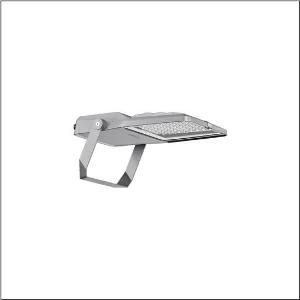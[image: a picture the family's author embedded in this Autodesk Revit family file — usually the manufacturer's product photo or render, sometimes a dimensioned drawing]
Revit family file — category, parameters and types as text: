
# Revit family: floodlight_fl_21_iq_mini___pl52_5xa7771c4d1a_1f8c
name_source: partatom
category: Lighting Fixtures
units: mm (PartAtom-declared; Revit-internal decimal feet)

## family parameters
Cut with Voids When Loaded = No
Host = Face
Light Source = No
Part Type = Normal
Room Calculation Point = No
Round Connector Dimension = Use Diameter
Shared = No

## types (1)
- --- (1 x LED, 12720 lm, 87.2 W, 4000K)
    Apparent Load = 87 VA
    CIE Flux Codes = 26 60 98 100 100
    Color Rendering = 70
    Color Temperature = 4000K
    Default Elevation = 1800 mm
    Description = Floodlight FL 21 iQ mini, floodlight, primary light control with lens, of PMMA, primary optical cover: protective disc, of toughened safety glass, transparent, light distribution: PL52, light emission: direct distribution, installation type: surface-mounted, LED, High Power LED, rated luminous flux: 12.720lm, luminous efficacy: 146lm/W, light colour: 740, colour temperature: 4000K, control: Auto-Match, Temp-Guard, Lumen-Switch, Night-Set, Smart-Wire, Light-Fading, Desk-Remote (wireless, voltage-free reading and setting of iQ features in the workshop via application-optimized NFC function/RFID function), optimised constant luminous flux control (CLO 2.0), with terminal, 6-pole, mains connection: 220..240V, AC, 50/60Hz, start of lifetime: 87W, end of service life: 92W, reduction: 40W, luminaire housing, of diecast aluminium, powder-coated, Siteco® metallic grey (DB 702S), corrosivity category C5 mid according to DIN EN ISO 12944, sealing non-destructively replaceable, mounting bracket, of steel, galvanised, powder-coated, Siteco® metallic grey (DB 702S), protection rating (complete): IP66, insulation class (complete): insulation class II (safety insulation), certification: CE, ENEC, VDE, protection symbol: D, impact resistance: IK08, permissible operating ambient temperature: -40..+40°C, permissible operating ambient temperature for outdoor applications: -40..+50°C, standard: DIN EN 12944, LABS conformity tested according to VDMA 24364:2018-05, packaging unit: 1 piece

Light Distribution: PL52
    Height = 70 mm
    Lamp = 1 x LED
    Lamp Light Flux = 12720 lm
    Lamp Power = 87.2 W
    Lamp count = 1
    Length = 485 mm
    Luminous efficacy = 146 lm/W
    Manufacturer = Siteco
    ModVariant = No
    Model = 5XA7771C4D1A
    Number of Poles = 1
    OnlyDefault = Yes
    Power Factor = 1
    Product Name = Floodlight FL 21 iQ mini | PL52
    Product group = floodlight | pylon annexe
    ProductGroupID = 6200
    Protection Class = Protection class II
    Protection Degree = IP 66
    RLX_Detail_Level = 1
    RLX_Emergency_Light_Flux = 0 lm
    RLX_Emergency_Type = 0
    RLX_Emergency_Type_DB = No
    RlxData = <blob elided: 96521 chars, md5=03fbc446>
    Socket = socket
    Standby Power = 0 W
    System Light Flux = 12720 lm
    System Power = 87 W
    Type Comments = factory setting: luminous flux: 100 % | dim-lin: 254 | 456 mA
    Type Image = l_1006845.jpg
    URL = http://relux.com
    VarID = @adj_096819
    Voltage = 0 V
    Weight = 0.00 kg
    Width = 337 mm

## geometry (parser evidence)
native form markers: Blend x4, Sweep x13
no freeform markers — native parametric forms only
